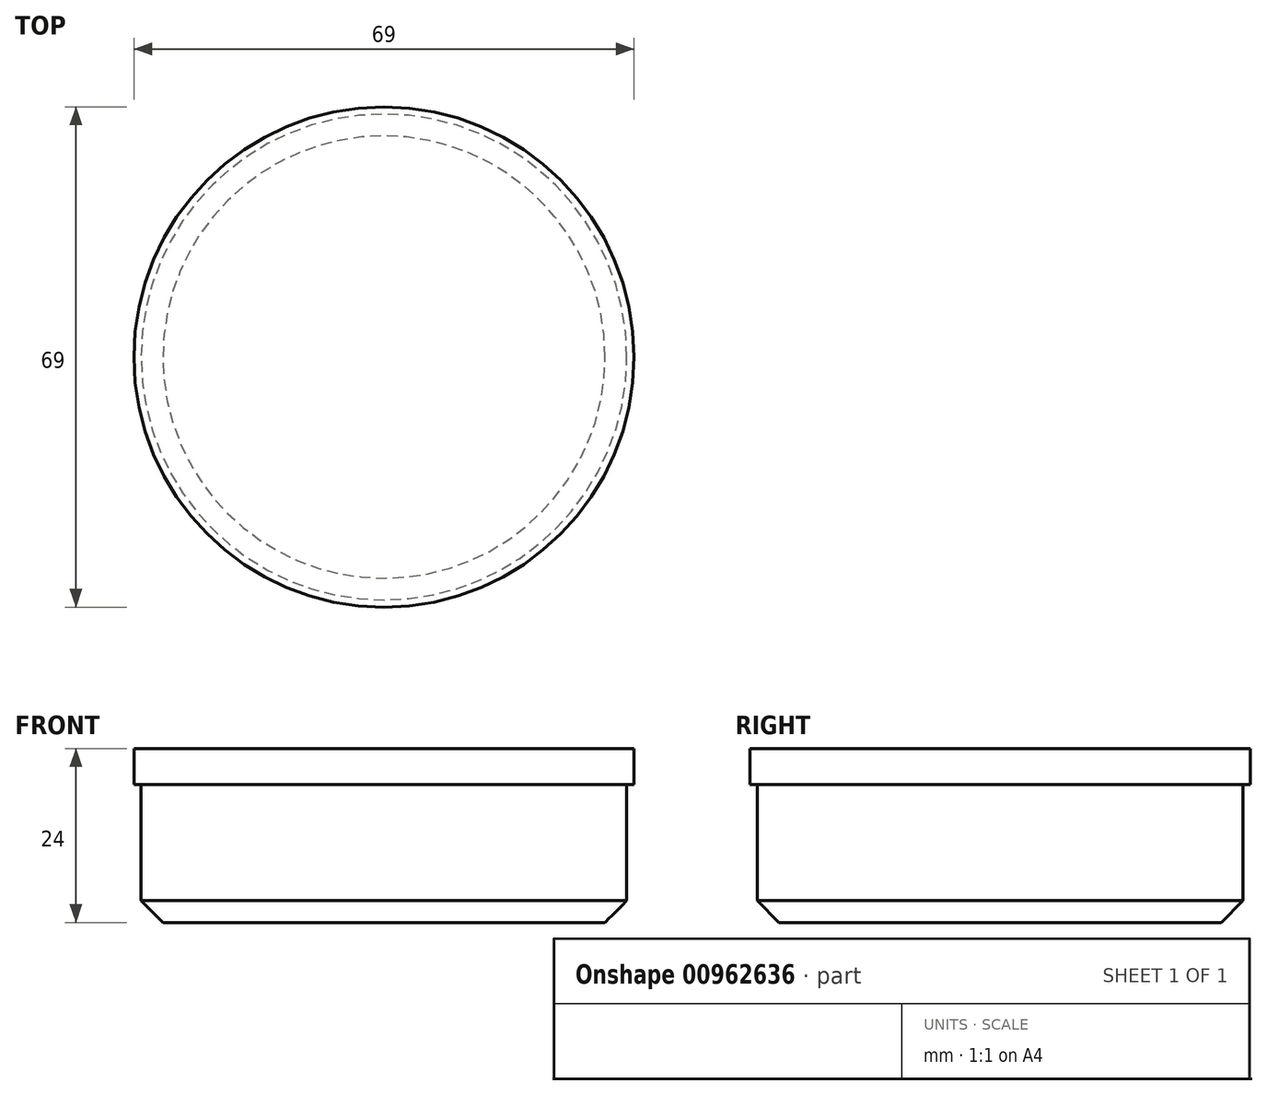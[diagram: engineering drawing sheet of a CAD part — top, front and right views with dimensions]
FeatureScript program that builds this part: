
annotation { "Feature Type Name" : "Feature", "Feature Type Description" : "" }
export const myFeature = defineFeature(function(context is Context, id is Id, definition is map)
    precondition{}
    {
        {
            var Q0;
            Q0=qCreatedBy(makeId("Top.planeOp"),FACE);
            var sketch = newSketch(context, id + "F0", { "sketchPlane" : qUnion([Q0])});
            skCircle(sketch, "E0", {"center": v(0, 0) * mm, "radius": 34 * mm});
            skCircle(sketch, "E1", {"center": v(0, 0) * mm, "radius": 33.5 * mm});
            skCircle(sketch, "E2", {"center": v(0, 0) * mm, "radius": 34.5 * mm});
            skSolve(sketch);
        }
        {
            var Q0;
            Q0 = qSketchRegion(id + "F0", true);
            var Q1;
            Q1=makeQuery(id+"F0.imprint","IMPRINT",FACE,{"disambiguationData":[TD([[makeQuery(id+"F0.imprint","IMPRINT",EDGE,{"derivedFrom":sQuery(id+"F0.wireOp",EDGE,"E1")}),1.0]])]});
            var Q2;
            Q2=makeQuery(id+"F0.imprint","IMPRINT",FACE,{"disambiguationData":[TD([[makeQuery(id+"F0.imprint","IMPRINT",EDGE,{"derivedFrom":sQuery(id+"F0.wireOp",EDGE,"E0")}),1.0]])]});
            extrude(context, id + "F1", {"entities" : qUnion([Q0, Q1, Q2]), "depth" : 5 * mm, "offsetDistance" : 25 * mm});
        }
        {
            var Q0;
            Q0=makeQuery(id+"F0.imprint","IMPRINT",FACE,{"disambiguationData":[TD([[makeQuery(id+"F0.imprint","IMPRINT",EDGE,{"derivedFrom":sQuery(id+"F0.wireOp",EDGE,"E1")}),1.0]])]});
            extrude(context, id + "F2", {"entities" : qUnion([Q0]), "operationType" : NewBodyOperationType.ADD, "oppositeDirection" : true, "depth" : 19 * mm, "offsetDistance" : 25 * mm});
        }
        {
            var Q0;
            Q0=makeQuery(id+"F1.opExtrude","CAP_FACE",FACE,{"disambiguationData":[OSD([sQuery(id+"F0.wireOp",EDGE,"E2")])],"isStart":false});
            var sketch = newSketch(context, id + "F3", { "sketchPlane" : qUnion([Q0])});
            skPoint(sketch, "E3.0", {"position": v(0, 0) * mm});
            skSolve(sketch);
        }
        {
            var Q0;
            Q0=makeQuery(id+"F2.opExtrude","CAP_EDGE",EDGE,{"disambiguationData":[OSD([sQuery(id+"F0.wireOp",EDGE,"E1")])],"isStart":false});
            chamfer(context, id + "F4", {"entities" : qUnion([Q0]), "width" : 3 * mm, "tangentPropagation" : true});
        }
    });
